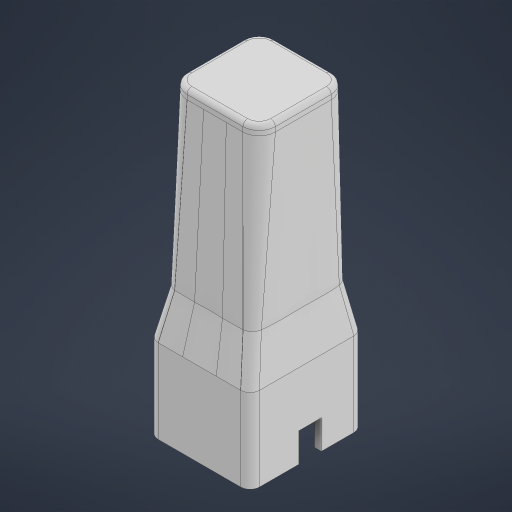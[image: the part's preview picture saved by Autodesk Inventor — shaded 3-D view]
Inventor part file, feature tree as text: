
AUTODESK INVENTOR PART (.ipt)
format: ipt  version: 2024.1 (Build 281209000, 209)  size: 5,960,704 bytes
history: native  units: mm
features: sketch x11, extrude x7, projected_geometry x6, loft x4, boolean_combine x4, other x3, fillet x2, plane x1
ambient origin geometry x8: Origin, YZ Plane, XZ Plane, XY Plane, X Axis, Y Axis, Z Axis, Center Point
bodies: Solid2 (feature_tree), Solid3 (feature_tree), Solid4 (feature_tree), Solid5 (feature_tree), Solid6 (feature_tree), Solid1 (feature_tree)
feature tree (38):
  other  "TubeHolder YN Continuation.ipt"
  extrude  "Extrusion1"  Depth=30.0mm
  fillet  "Fillet1"  Radius=30.0mm
  extrude  "Extrusion2"  Depth=3.0mm
  sketch  "Sketch3"  dims[d8=50.0mm d9=0.0mm d10=1.0mm]
  extrude  "Extrusion3"  Depth=1.0mm
  plane  "Work Plane1"
  sketch  "Sketch6"  dims[d15=3.0mm d16=28.0mm d17=0.0mm]
  sketch  "Sketch5"  dims[d13=1.0mm d14=1.0mm]
  loft  "Loft1"
  loft  "Loft2"
  boolean_combine  "Combine1"
  sketch  "Sketch7"  dims[d18=19.0mm d19=1.0mm]
  loft  "Loft3"
  loft  "Loft4"
  boolean_combine  "Combine2"
  extrude  "Extrusion4"  TaperAngle=0.0deg  [1 undecoded]
  extrude  "Extrusion5"  TaperAngle=0.0deg  [1 undecoded]
  boolean_combine  "Combine3"
  fillet  "Fillet2"  [1 undecoded]
  extrude  "Extrusion6"  TaperAngle=0.0deg  [1 undecoded]
  boolean_combine  "Combine4"
  extrude  "Extrusion7"  Depth=4.0mm
  other  "Solid1::TubeHolder YN Continuation.ipt"
  other  "TaggingFeature1"
  sketch  "Sketch1"  dims[d0=10.0mm d1=30.0mm d2=30.0mm]
  sketch  "Sketch2"  dims[d3=10.0mm d4=20.0mm d5=0.0mm d6=0.0mm d7=3.0mm]
  projected_geometry  "Projected Loop1"
  sketch  "Sketch4"  dims[d11=1.0mm d12=1.0mm]
  projected_geometry  "Projected Loop2"
  sketch  "Sketch8"  dims[d20=4.0mm d21=0.0mm d22=90.0deg]
  projected_geometry  "Projected Loop3"
  sketch  "Sketch9"  dims[d23=0.0mm d24=90.0deg d25=0.0mm d26=90.0deg d27=0.0mm d28=90.0deg]
  sketch  "Sketch10"  dims[d29=1.0mm d32=0.0mm d33=90.0deg]
  sketch  "Sketch11"  dims[d36=0.0mm d37=90.0deg d38=4.0mm d39=0.0mm d40=90.0deg d41=0.0mm d42=90.0deg d43=1.0mm d44=0.0mm d45=3.0mm d46=0.0mm d47=2.0mm d48=0.0mm d49=0.0mm d50=8.0mm d51=0.0mm]
  projected_geometry  "Project Cut Edges1"
  projected_geometry  "Project Cut Edges2"
  projected_geometry  "Project Cut Edges3"
note: 4 required parameter values undecoded (feature->parameter linkage not recoverable at this tier; creation-order binding heuristic only, values carry confidence <= 0.55)
